# Revit family: Sanitary_Taps&Mixers_Zurn-Industries_Z85500-XL
name_source: partatom
category: Plumbing Fixtures
units: mm (PartAtom-declared; Revit-internal decimal feet)

## family parameters
Cut with Voids When Loaded = No
Host = Face
Maintain Annotation Orientation = No
OmniClass Number = 23.45.55.17
OmniClass Title = Mixing Faucets
Part Type = Normal
Room Calculation Point = No
Round Connector Dimension = Use Radius
Shared = No

## types (1)
- Z85500-XL (Floor Mount Double Foot Pedal Valve)
    Activation Method = Manual Operated
    Assembly Code = D2010.60
    CW Connection = Yes
    CWFU = 1
    Default Elevation = 34 "
    Description = Floor-Mounted, Self-Closing, Double Foot Pedal Valve
    HW Connection = Yes
    HWFU = 1
    Height from Floor to Pedal = 1.063 "
    Height of Valve = 3.188 "
    Inlet Connection Diameter Size (inch) = 0.5 "
    Length of Pedal Valve = 5.063 "
    Main Material = Chrome-Plated Brass - Zurn - Polished
    Manufacturer = Zurn Water, LLC
    Manufacturer Brand = Zurn
    Model = Z85500-XL
    Modified Date = 02/20/2026
    Product Documentation Link = https://files.zurn.com
    Product Installation Sheet URL = https://files.zurn.com
    Product Page URL = https://www.zurn.com
    Product data URL = https://bimobject.com
    Repair Parts URL = https://files.zurn.com
    URL = http://www.zurn.com
    Vent Connection = No
    WFU = 0
    Waste Connection = No
    Width of Pedal Valve = 5.063 "

## geometry (parser evidence)
native form markers: Blend x6, Sweep x5
no freeform markers — native parametric forms only
